# Revit family: Typ.B_TP&N_Invicta_3_250A-UK-en
name_source: partatom
category: Electrical Equipment
units: mm (PartAtom-declared; Revit-internal decimal feet)

## family parameters
Cut with Voids When Loaded = No
Host = Face
Panel Configuration = Two Columns, Circuits Across
Part Type = Panelboard
Room Calculation Point = No
Round Connector Dimension = Use Diameter
Shared = No

## types (15) — shared parameters
Classification.Uniclass.Pr.Description = Control circuit device enclosures
Classification.Uniclass.Pr.Number = Pr_80_77_28_16
EF000003 - Mounting method = EV000384 - Surface mounted (plaster)
EF000008 - Width = 465 mm  [stored 1.52559 ft]
EF000049 - Depth = 166 mm  [stored 0.544619 ft]
EF000118 - With mounting plate = No
EF000339 - Type of cover = EV004216 - Door
EF001062 - EMC-version = No
EF001134 - DIN-rail = No
EF006244 - Transparent cover/door = No
EF015776 - Earthing terminal block = No
EF015777 - Neutral terminal block = No
EF015941 - Signal passing door = No
HG000002 - With door or cover = Yes
HG000003 - Range = Type B TP&N Distribution Boards
HG000005 - Thickness = 3 mm  [stored 0.00984252 ft]
HG000017 - Distance between poles = 18 mm  [stored 0.0590551 ft]
Manufacturer = Hager
Type Comments = Type B TP&N Distribution Boards
zero-valued in all types: Default Elevation, EF000218 - Built-in depth, EF000266 - Number of rows, EF000332 - Built-in height, EF000846 - Built-in width, EF001131 - Internal depth

## per-type parameters (varying)
| type | EF000007 - Colour | EF000040 - Height | EF000116 - RAL-number | EF001088 - Extension possible | EF001596 - Material housing | EF002950 - Width in number of modular spacings | EF004462 - Type of closure | EF005474 - Degree of protection (IP) | EF006306 - With lock | HG000004 - Manufacturer reference | Model |
| Surface mounted  W465 H1250 D165.5 24 Modular spacings - JK216BA3 |  | 1250 mm  [stored 4.10105 ft] |  | No |  | 24 |  |  | No | JK216BA3 | JK216BA3 |
| Surface mounted  W465 H1400 D165.5 27 Modular spacings - JK218BA3 |  | 1400 mm |  | No |  | 27 |  |  | No | JK218BA3 | JK218BA3 |
| Surface mounted  W465 H950 D165.5 12 Modular spacings - JK208B |  | 950 mm  [stored 3.1168 ft] |  | No |  | 12 |  |  | No | JK208B | JK208B |
| Surface mounted IP30 W465 H1100 D165.5 18 Modular spacings - JK212B | EV000154 - Other | 1100 mm | 7035 | No | EV000179 - Steel | 18 | EV000154 - Other | EV006410 - IP30 | Yes | JK212B | JK212B |
| Surface mounted IP30 W465 H1100 D165.5 18 Modular spacings - JK212BA3 |  | 1100 mm | 7035 | Yes | EV000179 - Steel | 18 | EV000154 - Other | EV006410 - IP30 | No | JK212BA3 | JK212BA3 |
| Surface mounted IP30 W465 H1100 D165.5 18 Modular spacings - JK212BG | EV000154 - Other | 1100 mm | 7035 | No | EV000179 - Steel | 18 | EV000154 - Other | EV006410 - IP30 | Yes | JK212BG | JK212BG |
| Surface mounted IP30 W465 H1250 D165.5 24 Modular spacings - JK216B | EV000154 - Other | 1250 mm  [stored 4.10105 ft] | 7035 | No | EV000179 - Steel | 24 | EV000154 - Other | EV006410 - IP30 | Yes | JK216B | JK216B |
| Surface mounted IP30 W465 H1250 D165.5 24 Modular spacings - JK216BG | EV000154 - Other | 1250 mm  [stored 4.10105 ft] | 7035 | No | EV000179 - Steel | 24 | EV000154 - Other | EV006410 - IP30 | Yes | JK216BG | JK216BG |
| Surface mounted IP30 W465 H1400 D165.5 27 Modular spacings - JK218B | EV000154 - Other | 1400 mm | 7035 | No | EV000179 - Steel | 27 | EV000154 - Other | EV006410 - IP30 | Yes | JK218B | JK218B |
| Surface mounted IP30 W465 H1400 D165.5 27 Modular spacings - JK218BG | EV000154 - Other | 1400 mm | 7035 | No | EV000179 - Steel | 27 | EV000154 - Other | EV006410 - IP30 | Yes | JK218BG | JK218BG |
| Surface mounted IP30 W465 H1550 D165.5 36 Modular spacings - JK224B | EV000154 - Other | 1550 mm | 7035 | No | EV000179 - Steel | 36 | EV000154 - Other | EV006410 - IP30 | Yes | JK224B | JK224B |
| Surface mounted IP30 W465 H1550 D165.5 36 Modular spacings - JK224BA3 |  | 1550 mm | 7035 | Yes | EV000179 - Steel | 36 | EV000154 - Other | EV006410 - IP30 | No | JK224BA3 | JK224BA3 |
| Surface mounted IP30 W465 H1550 D165.5 36 Modular spacings - JK224BG | EV000154 - Other | 1550 mm | 7035 | No | EV000179 - Steel | 36 | EV000154 - Other | EV006410 - IP30 | Yes | JK224BG | JK224BG |
| Surface mounted IP30 W465 H950 D165.5 12 Modular spacings - JK208BA3 |  | 950 mm  [stored 3.1168 ft] | 7035 | Yes | EV000179 - Steel | 12 | EV000154 - Other | EV006410 - IP30 | No | JK208BA3 | JK208BA3 |
| Surface mounted IP30 W465 H950 D165.5 12 Modular spacings - JK208BG | EV000154 - Other | 950 mm  [stored 3.1168 ft] | 7035 | No | EV000179 - Steel | 12 | EV000154 - Other | EV006410 - IP30 | Yes | JK208BG | JK208BG |

note: [stored X ft] marks values corroborated as IEEE doubles in the binary element streams (Revit-internal decimal feet)

## geometry (parser evidence)
native form markers: Sweep x8
no freeform markers — native parametric forms only
